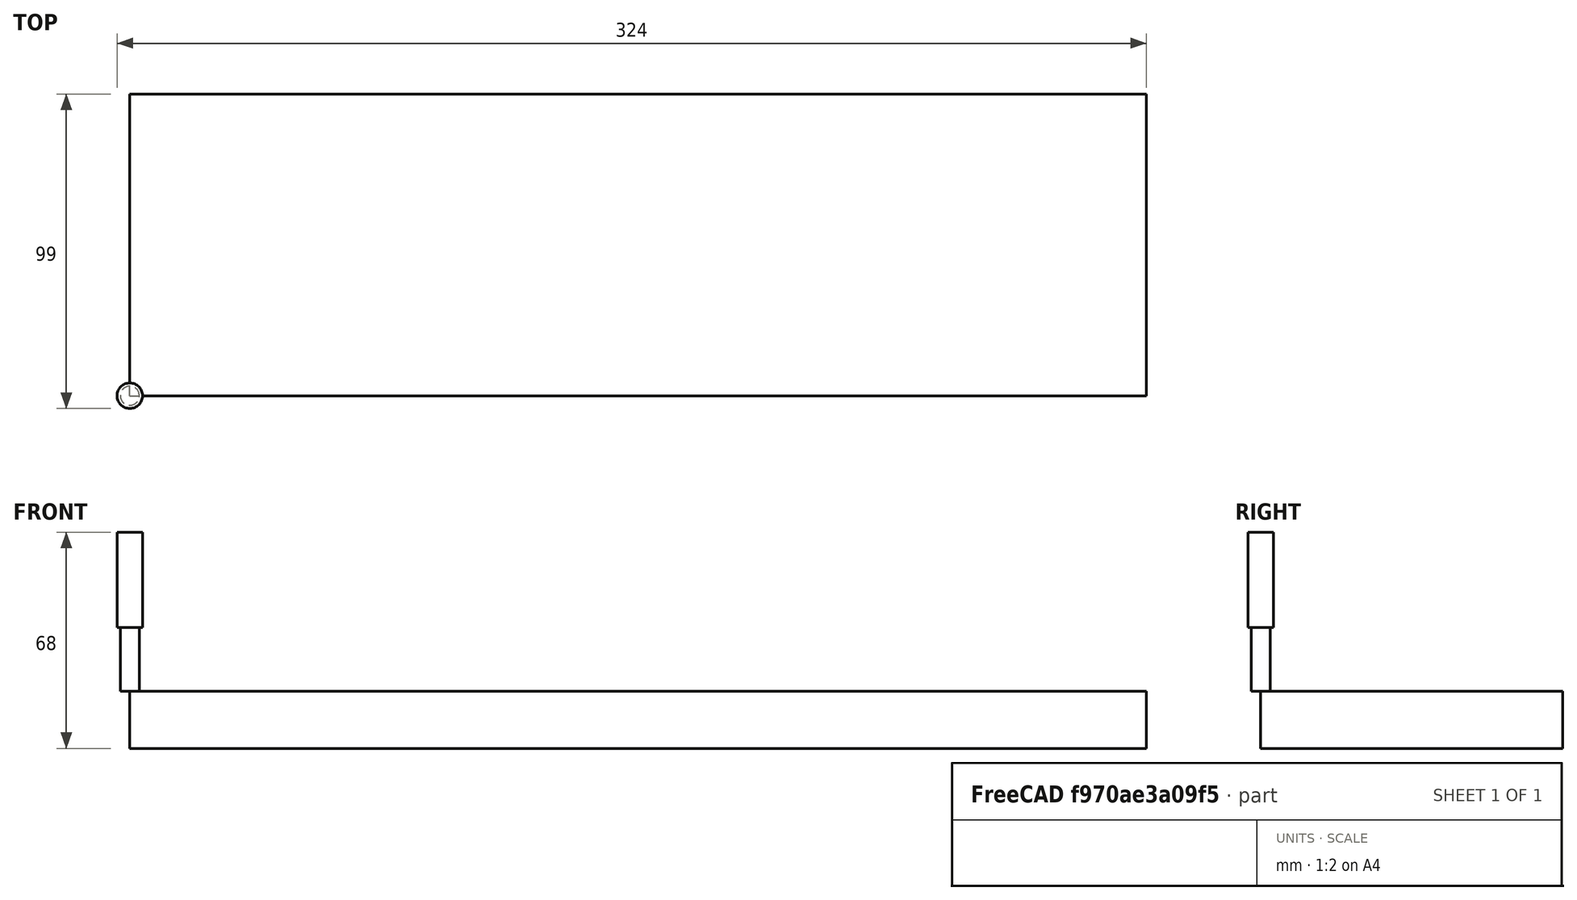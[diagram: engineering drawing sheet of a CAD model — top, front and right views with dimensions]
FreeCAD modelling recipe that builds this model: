
FCSTD DOCUMENT  (FreeCAD 0.22R34789 (Git))
Label: base_right
License: All rights reserved
LicenseURL: http://en.wikipedia.org/wiki/All_rights_reserved
objects: Path::FeaturePython×7, Part::FeaturePython×4, App::DocumentObjectGroup×3, App::FeaturePython×1
note: 11 computed .brp shape members not serialized (recipe doc carries the construction recipe); baked Part::Feature solids carry a one-line shape summary decoded from their .brp

FEATURE [Part::FeaturePython] b_drill_press_table_001_  label="drill_press_table_base_side_right_001"  # a2plus imported part (geometry in sourceFile) (typed FeaturePython)
  Placement = pos=(0,0,0) rot=(0.57735,-0.57735,-0.57735;4.18879rad)
  a2p_Version = 0.4.61
  fixedPosition = true
  objectType = a2pPart
  sourceFile = ./../drill_press_table.FCStd
  sourcePart = base_side_right
  subassemblyImport = false
  timeLastImport = 1.69969e+09
  updateColors = true
FEATURE [App::FeaturePython] SetupSheet  # Path/CAM operation (typed FeaturePython)
  ClearanceHeightExpression = OpStockZMax+SetupSheet.ClearanceHeightOffset
  ClearanceHeightOffset = 5
  CoolantMode = 0
  CoolantModes = None | Flood | Mist
  FinalDepthExpression = OpFinalDepth
  HorizRapid = 0
  SafeHeightExpression = OpStockZMax+SetupSheet.SafeHeightOffset
  SafeHeightOffset = 3
  StartDepthExpression = OpStartDepth
  StepDownExpression = OpToolDiameter
  VertRapid = 0
FEATURE [Part::FeaturePython] Clone  label="Model-drill_press_table_base_side_right_001"  # Draft clone (typed FeaturePython)
  AttacherType = Attacher::AttachEngine3D
  Fuse = false
  Objects = -> [b_drill_press_table_001_]
  PathResource = Model
  Placement = pos=(372,85,113) rot=(0.57735,-0.57735,-0.57735;4.18879rad)
  Scale = (1,1,1)
FEATURE [App::DocumentObjectGroup] Model
  Group = -> [Clone]
FEATURE [Part::FeaturePython] Stock  # WARN: FeaturePython — macro-defined, semantics opaque (R4)
  Base = -> Model
  ExtXneg = 10
  ExtXpos = 10
  ExtYneg = 10
  ExtYpos = 10
  ExtZneg = 0
  ExtZpos = 0
  Placement = pos=(10,10,-18) rot=(0,0,1;0rad)
  StockType = FromBase
FEATURE [Part::FeaturePython] Endmill_D_6__H_20__S_8  label="Endmill D=6, H=20, S=8"  # Path/CAM toolbit (typed FeaturePython)
  BitPropertyNames = Chipload | CuttingEdgeHeight | Diameter | Flutes | Length | Material | ShankDiameter | SpindleDirection
  BitShape = <userpath>/.local/share/FreeCAD/Macro/Tools/Shape/endmill.fcstd
  Chipload = 0
  CuttingEdgeHeight = 20
  Diameter = 6
  File = <userpath>/.local/share/FreeCAD/Macro/Tools/Bit/fbe41074-7b3e-11ee-b334-02422c3495f2.fctb
  Flutes = 2
  Length = 50
  Material = 0
  ShankDiameter = 8
  ShapeName = endmill
  SpindleDirection = 0
FEATURE [Path::FeaturePython] TC__Endmill_D_6__H_20__S_8  label="TC: Endmill D=6, H=20, S=8"  # Path/CAM operation (typed FeaturePython)
  HorizFeed = 15
  HorizRapid = 0
  SpindleDir = 0
  SpindleSpeed = 0
  Tool = -> Endmill_D_6__H_20__S_8
  ToolNumber = 16
  VertFeed = 1
  VertRapid = 0
  expr: HorizRapid = SetupSheet.HorizRapid
  expr: VertRapid = SetupSheet.VertRapid
FEATURE [App::DocumentObjectGroup] Tools
  Group = -> [TC__Endmill_D_6__H_20__S_8]
FEATURE [Path::FeaturePython] Pocket_Shape  # Path/CAM operation (typed FeaturePython)
  Active = true
  AreaParams:
    Tolerance = 1e-07
    FitArcs = True
    Simplify = False
    CleanDistance = 0.0
    Accuracy = 0.01
    Unit = 1.0
    MinArcPoints = 4
    MaxArcPoints = 100
    ClipperScale = 10000000.0
    Fill = 0
    Coplanar = 0
    Reorient = True
    Outline = False
    Explode = False
    OpenMode = 0
    Deflection = 0.01
    SubjectFill = 0
    ClipFill = 0
    Offset = 0.0
    ExtraPass = 0
    Stepover = 0.0
    LastStepover = 0.0
    JoinType = 0
    EndType = 0
    MiterLimit = 2.0
    RoundPrecision = 0.0
    PocketMode = 2
    ToolRadius = 3.0
    PocketExtraOffset = -0.8
    PocketStepover = 4.800000000000001
    PocketLastStepover = 0.0
    FromCenter = True
    Angle = 45.0
    AngleShift = 0.0
    Shift = 0.0
    Thicken = False
    SectionCount = -1
    Stepdown = 1.0
    SectionOffset = 0.0
    SectionTolerance = 1e-07
    SectionMode = 2
    Project = False
  Base = -> [Clone]
  ClearanceHeight = 5
  CoolantMode = 0
  CutMode = 0
  CycleTime = 00:07:29
  ExtensionCorners = true
  ExtensionFeature = -> [Clone]
  ExtensionLengthDefault = 4
  ExtraOffset = -0.8
  FinalDepth = -6.5
  FinishDepth = 0
  KeepToolDown = false
  MinTravel = false
  OffsetPattern = 1
  OpFinalDepth = -6
  OpStartDepth = 0
  OpStockZMax = -3.6e-15
  OpStockZMin = -18
  OpToolDiameter = 6
  PathParams = {'orientation': 1, 'feedrate': 15.0, 'feedrate_v': 1.0, 'verbose': True, 'resume_height': 2.9999999999999964, 'retraction': 4.9999999999999964, 'return_end': True, 'preamble': False}
  PocketLastStepOver = 0
  SafeHeight = 3
  SplitArcs = false
  StartAt = 0
  StartDepth = 0
  StartPoint = (0,0,0)
  StepDown = 2
  StepOver = 80
  ToolController = -> TC__Endmill_D_6__H_20__S_8
  UseOutline = false
  UseRestMachining = false
  UseStartPoint = false
  ZigZagAngle = 45
  expr: ClearanceHeight = OpStockZMax + SetupSheet.ClearanceHeightOffset
  expr: ExtensionLengthDefault = OpToolDiameter / 2 + 1 mm
  expr: FinalDepth = OpFinalDepth - 0.5 mm
  expr: SafeHeight = OpStockZMax + SetupSheet.SafeHeightOffset
  expr: StartDepth = OpStartDepth
  expr: StepDown = OpToolDiameter / 3
FEATURE [Path::FeaturePython] Pocket_Shape001  # Path/CAM operation (typed FeaturePython)
  Active = true
  AreaParams:
    Tolerance = 1e-07
    FitArcs = True
    Simplify = False
    CleanDistance = 0.0
    Accuracy = 0.01
    Unit = 1.0
    MinArcPoints = 4
    MaxArcPoints = 100
    ClipperScale = 10000000.0
    Fill = 0
    Coplanar = 0
    Reorient = True
    Outline = False
    Explode = False
    OpenMode = 0
    Deflection = 0.01
    SubjectFill = 0
    ClipFill = 0
    Offset = 0.0
    ExtraPass = 0
    Stepover = 0.0
    LastStepover = 0.0
    JoinType = 0
    EndType = 0
    MiterLimit = 2.0
    RoundPrecision = 0.0
    PocketMode = 2
    ToolRadius = 3.0
    PocketExtraOffset = -1.0
    PocketStepover = 4.800000000000001
    PocketLastStepover = 0.0
    FromCenter = True
    Angle = 45.0
    AngleShift = 0.0
    Shift = 0.0
    Thicken = False
    SectionCount = -1
    Stepdown = 1.0
    SectionOffset = 0.0
    SectionTolerance = 1e-07
    SectionMode = 2
    Project = False
  Base = -> [Clone]
  ClearanceHeight = 5
  CoolantMode = 0
  CutMode = 0
  CycleTime = 00:09:00
  ExtensionCorners = true
  ExtensionFeature = -> [Clone]
  ExtensionLengthDefault = 3
  ExtraOffset = -1
  FinalDepth = -6.5
  FinishDepth = 0
  KeepToolDown = false
  MinTravel = false
  OffsetPattern = 1
  OpFinalDepth = -6
  OpStartDepth = 0
  OpStockZMax = -3.6e-15
  OpStockZMin = -18
  OpToolDiameter = 6
  PathParams = {'orientation': 1, 'feedrate': 15.0, 'feedrate_v': 1.0, 'verbose': True, 'resume_height': 2.9999999999999964, 'retraction': 4.9999999999999964, 'return_end': True, 'preamble': False}
  PocketLastStepOver = 0
  SafeHeight = 3
  SplitArcs = false
  StartAt = 0
  StartDepth = 0
  StartPoint = (0,0,0)
  StepDown = 2
  StepOver = 80
  ToolController = -> TC__Endmill_D_6__H_20__S_8
  UseOutline = false
  UseRestMachining = false
  UseStartPoint = false
  ZigZagAngle = 45
  expr: ClearanceHeight = OpStockZMax + SetupSheet.ClearanceHeightOffset
  expr: ExtensionLengthDefault = OpToolDiameter / 2
  expr: FinalDepth = OpFinalDepth - 0.5 mm
  expr: SafeHeight = OpStockZMax + SetupSheet.SafeHeightOffset
  expr: StartDepth = OpStartDepth
  expr: StepDown = OpToolDiameter / 3
FEATURE [Path::FeaturePython] Pocket_Shape002  # Path/CAM operation (typed FeaturePython)
  Active = true
  AreaParams:
    Tolerance = 1e-07
    FitArcs = True
    Simplify = False
    CleanDistance = 0.0
    Accuracy = 0.01
    Unit = 1.0
    MinArcPoints = 4
    MaxArcPoints = 100
    ClipperScale = 10000000.0
    Fill = 0
    Coplanar = 0
    Reorient = True
    Outline = False
    Explode = False
    OpenMode = 0
    Deflection = 0.01
    SubjectFill = 0
    ClipFill = 0
    Offset = 0.0
    ExtraPass = 0
    Stepover = 0.0
    LastStepover = 0.0
    JoinType = 0
    EndType = 0
    MiterLimit = 2.0
    RoundPrecision = 0.0
    PocketMode = 2
    ToolRadius = 3.0
    PocketExtraOffset = -0.6
    PocketStepover = 4.800000000000001
    PocketLastStepover = 0.0
    FromCenter = True
    Angle = 45.0
    AngleShift = 0.0
    Shift = 0.0
    Thicken = False
    SectionCount = -1
    Stepdown = 1.0
    SectionOffset = 0.0
    SectionTolerance = 1e-07
    SectionMode = 2
    Project = False
  Base = -> [Clone]
  ClearanceHeight = 5
  CoolantMode = 0
  CutMode = 0
  CycleTime = 00:07:55
  ExtensionCorners = true
  ExtensionFeature = -> [Clone]
  ExtensionLengthDefault = 3
  ExtraOffset = -0.6
  FinalDepth = -6.5
  FinishDepth = 0
  KeepToolDown = false
  MinTravel = false
  OffsetPattern = 1
  OpFinalDepth = -6
  OpStartDepth = 0
  OpStockZMax = -3.6e-15
  OpStockZMin = -18
  OpToolDiameter = 6
  PathParams = {'orientation': 1, 'feedrate': 15.0, 'feedrate_v': 1.0, 'verbose': True, 'resume_height': 2.9999999999999964, 'retraction': 4.9999999999999964, 'return_end': True, 'preamble': False}
  PocketLastStepOver = 0
  SafeHeight = 3
  SplitArcs = false
  StartAt = 0
  StartDepth = 0
  StartPoint = (0,0,0)
  StepDown = 2
  StepOver = 80
  ToolController = -> TC__Endmill_D_6__H_20__S_8
  UseOutline = false
  UseRestMachining = false
  UseStartPoint = false
  ZigZagAngle = 45
  expr: ClearanceHeight = OpStockZMax + SetupSheet.ClearanceHeightOffset
  expr: ExtensionLengthDefault = OpToolDiameter / 2
  expr: FinalDepth = OpFinalDepth - 0.5 mm
  expr: SafeHeight = OpStockZMax + SetupSheet.SafeHeightOffset
  expr: StartDepth = OpStartDepth
  expr: StepDown = OpToolDiameter / 3
FEATURE [Path::FeaturePython] Profile  # Path/CAM operation (typed FeaturePython)
  Active = true
  AreaParams:
    Tolerance = 1e-07
    FitArcs = True
    Simplify = False
    CleanDistance = 0.0
    Accuracy = 0.01
    Unit = 1.0
    MinArcPoints = 4
    MaxArcPoints = 100
    ClipperScale = 10000000.0
    Fill = 0
    Coplanar = 0
    Reorient = True
    Outline = False
    Explode = False
    OpenMode = 0
    Deflection = 0.01
    SubjectFill = 0
    ClipFill = 0
    Offset = 3.0
    ExtraPass = 0
    Stepover = 0.0
    LastStepover = 0.0
    JoinType = 0
    EndType = 0
    MiterLimit = 2.0
    RoundPrecision = 0.0
    PocketMode = 0
    ToolRadius = 1.0
    PocketExtraOffset = 0.0
    PocketStepover = 0.0
    PocketLastStepover = 0.0
    FromCenter = False
    Angle = 45.0
    AngleShift = 0.0
    Shift = 0.0
    Thicken = False
    SectionCount = -1
    Stepdown = 1.0
    SectionOffset = 0.0
    SectionTolerance = 1e-07
    SectionMode = 2
    Project = False
  ClearanceHeight = 5
  CoolantMode = 0
  CycleTime = 00:09:45
  Direction = 0
  FinalDepth = -20
  HandleMultipleFeatures = 0
  JoinType = 0
  MiterLimit = 0.1
  OffsetExtra = 0
  OpFinalDepth = -18
  OpStartDepth = -3.6e-15
  OpStockZMax = -3.6e-15
  OpStockZMin = -18
  OpToolDiameter = 6
  PathParams = {'orientation': 1, 'feedrate': 15.0, 'feedrate_v': 1.0, 'verbose': True, 'resume_height': 2.9999999999999964, 'retraction': 4.9999999999999964, 'return_end': True, 'preamble': False}
  SafeHeight = 3
  Side = 0
  SplitArcs = false
  StartDepth = -3.6e-15
  StartPoint = (0,0,0)
  StepDown = 2
  ToolController = -> TC__Endmill_D_6__H_20__S_8
  UseComp = true
  UseStartPoint = false
  processCircles = false
  processHoles = false
  processPerimeter = true
  expr: ClearanceHeight = OpStockZMax + SetupSheet.ClearanceHeightOffset
  expr: FinalDepth = OpFinalDepth - 2 mm
  expr: SafeHeight = OpStockZMax + SetupSheet.SafeHeightOffset
  expr: StartDepth = OpStartDepth
  expr: StepDown = OpToolDiameter / 3
FEATURE [Path::FeaturePython] DressupTag  # Path/CAM operation (typed FeaturePython)
  Angle = 45
  Base = -> Profile
  Height = 8
  Positions = (4) [(235,7,0),(85,7,0),(85,88,0),(235,88,0)]
  Radius = 0
  SegmentationFactor = 50
  Width = 12
FEATURE [App::DocumentObjectGroup] Operations
  Group = -> [Pocket_Shape,Pocket_Shape001,Pocket_Shape002,DressupTag]
FEATURE [Path::FeaturePython] Job  # Path/CAM operation (typed FeaturePython)
  CycleTime = 00:34:09
  Fixtures = G54
  GeometryTolerance = 0.01
  JobType = 0
  Model = -> Model
  Operations = -> Operations
  OrderOutputBy = 0
  PostProcessor = 3
  PostProcessorOutputFile = %D/%d.gcode
  SetupSheet = -> SetupSheet
  SplitOutput = false
  Stock = -> Stock
  Tools = -> Tools
